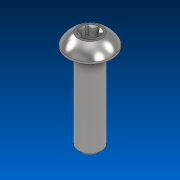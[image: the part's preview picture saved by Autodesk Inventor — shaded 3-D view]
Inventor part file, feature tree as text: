
AUTODESK INVENTOR PART (.ipt)
format: ipt  version: 2022.2 (Build 262287000, 287)  size: 181,760 bytes
history: native  units: in
note: dims shown in document units (in); Inventor stores cm internally (conversion verified against a paired STEP export)
features: direct_edit x1, chamfer x1, move_body x1
ambient origin geometry x8: Origin, YZ Plane, XZ Plane, XY Plane, X Axis, Y Axis, Z Axis, Center Point
bodies: Solid1 (feature_tree)
feature tree (3):
  direct_edit  "Direct Edit1"
  chamfer  "Chamfer2"  [1 undecoded]
  move_body  "Move1"
note: 1 required parameter value undecoded (feature->parameter linkage not recoverable at this tier; creation-order binding heuristic only, values carry confidence <= 0.55)
